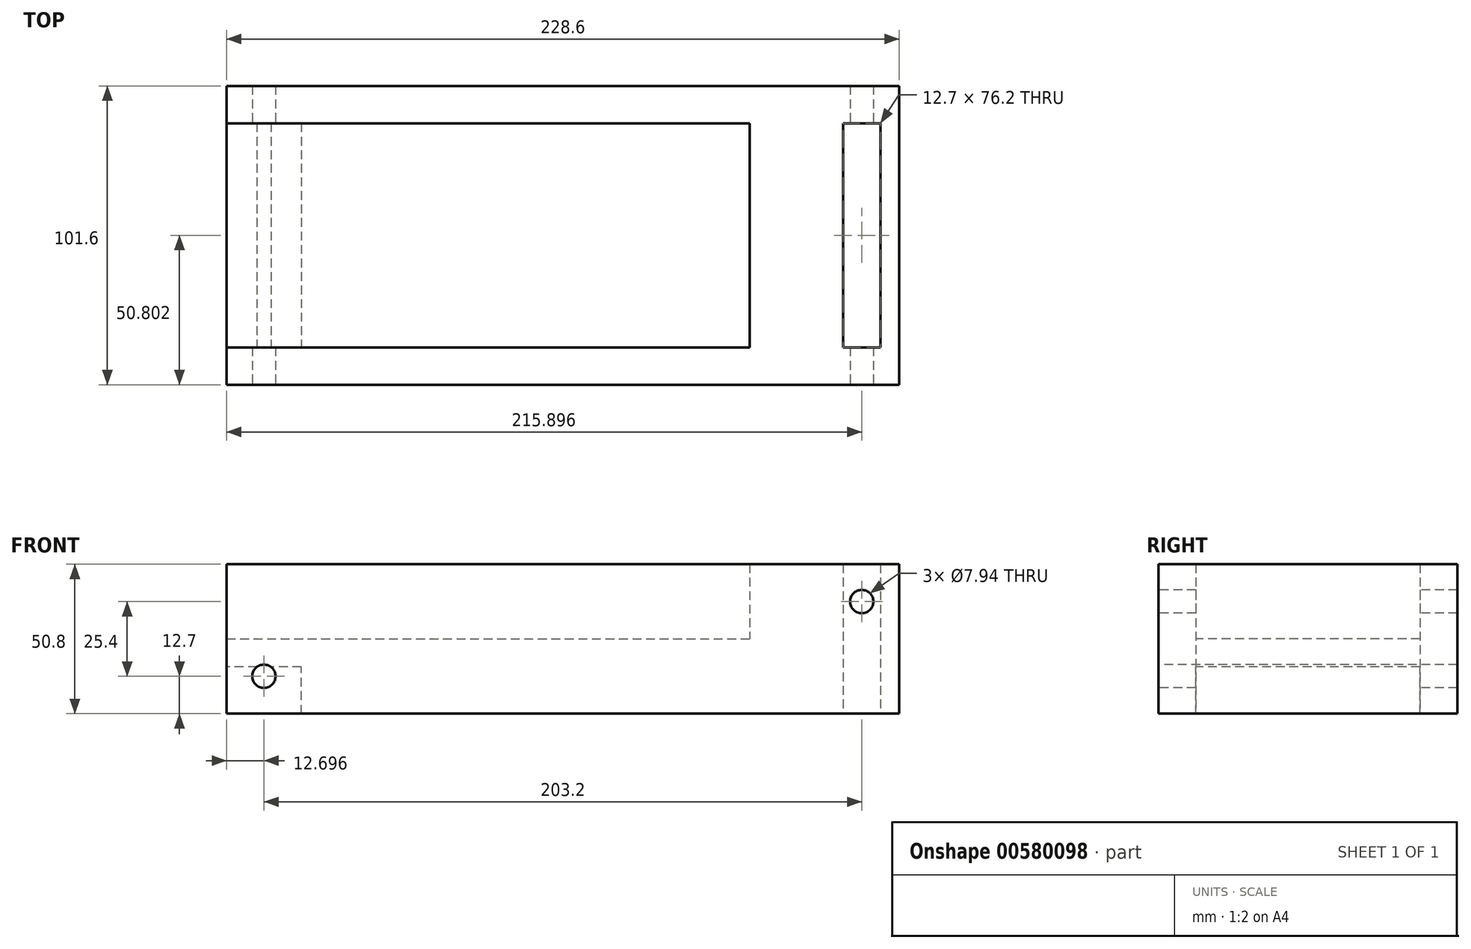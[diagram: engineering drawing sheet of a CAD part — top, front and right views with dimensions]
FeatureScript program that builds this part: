
annotation { "Feature Type Name" : "Feature", "Feature Type Description" : "" }
export const myFeature = defineFeature(function(context is Context, id is Id, definition is map)
    precondition{}
    {
        {
            var Q0;
            Q0=qCreatedBy(makeId("Top.planeOp"),FACE);
            var sketch = newSketch(context, id + "F0", { "sketchPlane" : qUnion([Q0])});
            skLineSegment(sketch, "E0.bottom", {"start": v(-74.58, 53.35) * mm, "end": v(154.02, 53.35) * mm});
            skLineSegment(sketch, "E0.top", {"start": v(-74.58, -48.25) * mm, "end": v(154.02, -48.25) * mm});
            skLineSegment(sketch, "E0.left", {"start": v(-74.58, 53.35) * mm, "end": v(-74.58, -48.25) * mm});
            skLineSegment(sketch, "E0.right", {"start": v(154.02, 53.35) * mm, "end": v(154.02, -48.25) * mm});
            skLineSegment(sketch, "E1.bottom", {"start": v(134.97, 40.65) * mm, "end": v(147.67, 40.65) * mm});
            skLineSegment(sketch, "E1.top", {"start": v(134.97, -35.55) * mm, "end": v(147.67, -35.55) * mm});
            skLineSegment(sketch, "E1.left", {"start": v(134.97, 40.65) * mm, "end": v(134.97, -35.55) * mm});
            skLineSegment(sketch, "E1.right", {"start": v(147.67, 40.65) * mm, "end": v(147.67, -35.55) * mm});
            skLineSegment(sketch, "E2.bottom", {"start": v(-74.58, 40.65) * mm, "end": v(103.22, 40.65) * mm});
            skLineSegment(sketch, "E2.top", {"start": v(-74.58, -35.55) * mm, "end": v(103.22, -35.55) * mm});
            skLineSegment(sketch, "E2.left", {"start": v(-74.58, 40.65) * mm, "end": v(-74.58, -35.55) * mm});
            skLineSegment(sketch, "E2.right", {"start": v(103.22, 40.65) * mm, "end": v(103.22, -35.55) * mm});
            skSolve(sketch);
        }
        {
            var Q0;
            {var subQ1=sQuery(id+"F0.wireOp",EDGE,"E0.bottom");Q0=makeQuery(id+"F0.imprint","IMPRINT",FACE,{"disambiguationData":[TD([[makeQuery(id+"F0.imprint","IMPRINT",EDGE,{"derivedFrom":subQ1}),-1.0]])]});}
            extrude(context, id + "F1", {"entities" : qUnion([Q0]), "depth" : 50.8 * mm, "symmetric" : true});
        }
        {
            var Q0;
            Q0=makeQuery(id+"F0.imprint","IMPRINT",FACE,{"disambiguationData":[TD([[makeQuery(id+"F0.imprint","IMPRINT",EDGE,{"derivedFrom":sQuery(id+"F0.wireOp",EDGE,"E2.bottom")}),-1.0]])]});
            extrude(context, id + "F2", {"entities" : qUnion([Q0]), "operationType" : NewBodyOperationType.ADD, "oppositeDirection" : true, "depth" : 25.4 * mm});
        }
        {
            var Q0;
            Q0=makeQuery(id+"F1.opExtrude","SWEPT_FACE",FACE,{"disambiguationData":[OSD([sQuery(id+"F0.wireOp",EDGE,"E0.top")])]});
            var sketch = newSketch(context, id + "F3", { "sketchPlane" : qUnion([Q0])});
            skCircle(sketch, "E3", {"center": v(141.32, 12.7) * mm, "radius": 3.97 * mm});
            skSolve(sketch);
        }
        {
            var Q0;
            Q0=qSketchRegion(id+"F3",true);
            extrude(context, id + "F4", {"entities" : qUnion([Q0]), "operationType" : NewBodyOperationType.REMOVE, "oppositeDirection" : true, "depth" : 254 * mm});
        }
        {
            var Q0;
            Q0=makeQuery(id+"F1.opExtrude","SWEPT_FACE",FACE,{"disambiguationData":[OSD([sQuery(id+"F0.wireOp",EDGE,"E0.top")])]});
            var sketch = newSketch(context, id + "F5", { "sketchPlane" : qUnion([Q0])});
            skCircle(sketch, "E4", {"center": v(-61.88, -12.7) * mm, "radius": 3.97 * mm});
            skSolve(sketch);
        }
        {
            var Q0;
            Q0=qSketchRegion(id+"F5",true);
            extrude(context, id + "F6", {"entities" : qUnion([Q0]), "operationType" : NewBodyOperationType.REMOVE, "oppositeDirection" : true, "depth" : 152.4 * mm});
        }
        {
            var Q0;
            {var subQ0=sQuery(id+"F0.wireOp",EDGE,"E2.left");var subQ1=sQuery(id+"F0.wireOp",EDGE,"E0.left");Q0=makeQuery(id+"F2.boolean.opBoolean","MERGE",FACE,{"derivedFrom":[makeQuery(id+"F1.opExtrude","SWEPT_FACE",FACE,{"disambiguationData":[OSD([subQ1]),TDD([makeQuery(id+"F0.imprint","IMPRINT",EDGE,{"disambiguationData":[TD([[makeQuery(id+"F0.imprint","INTERSECT",VERTEX,{"derivedFrom":[sQuery(id+"F0.wireOp",EDGE,"E0.bottom"),subQ1]}),-1.0]])],"derivedFrom":subQ1})])]}),makeQuery(id+"F1.opExtrude","SWEPT_FACE",FACE,{"disambiguationData":[OSD([subQ1]),TDD([makeQuery(id+"F0.imprint","IMPRINT",EDGE,{"disambiguationData":[TD([[makeQuery(id+"F0.imprint","INTERSECT",VERTEX,{"derivedFrom":[sQuery(id+"F0.wireOp",EDGE,"E0.top"),subQ1]}),1.0]])],"derivedFrom":subQ1})])]}),makeQuery(id+"F2.opExtrude","SWEPT_FACE",FACE,{"disambiguationData":[OSD([subQ0])]})]});}
            var sketch = newSketch(context, id + "F7", { "sketchPlane" : qUnion([Q0])});
            skLineSegment(sketch, "E5.bottom", {"start": v(-40.65, -25.4) * mm, "end": v(35.55, -25.4) * mm});
            skLineSegment(sketch, "E5.top", {"start": v(-40.65, -9.53) * mm, "end": v(35.55, -9.52) * mm});
            skLineSegment(sketch, "E5.left", {"start": v(-40.65, -25.4) * mm, "end": v(-40.65, -9.53) * mm});
            skLineSegment(sketch, "E5.right", {"start": v(35.55, -25.4) * mm, "end": v(35.55, -9.52) * mm});
            skSolve(sketch);
        }
        {
            var Q0;
            Q0=qSketchRegion(id+"F7",true);
            extrude(context, id + "F8", {"entities" : qUnion([Q0]), "operationType" : NewBodyOperationType.REMOVE, "oppositeDirection" : true, "depth" : 25.4 * mm, "offsetDistance" : 25.4 * mm});
        }
    });
